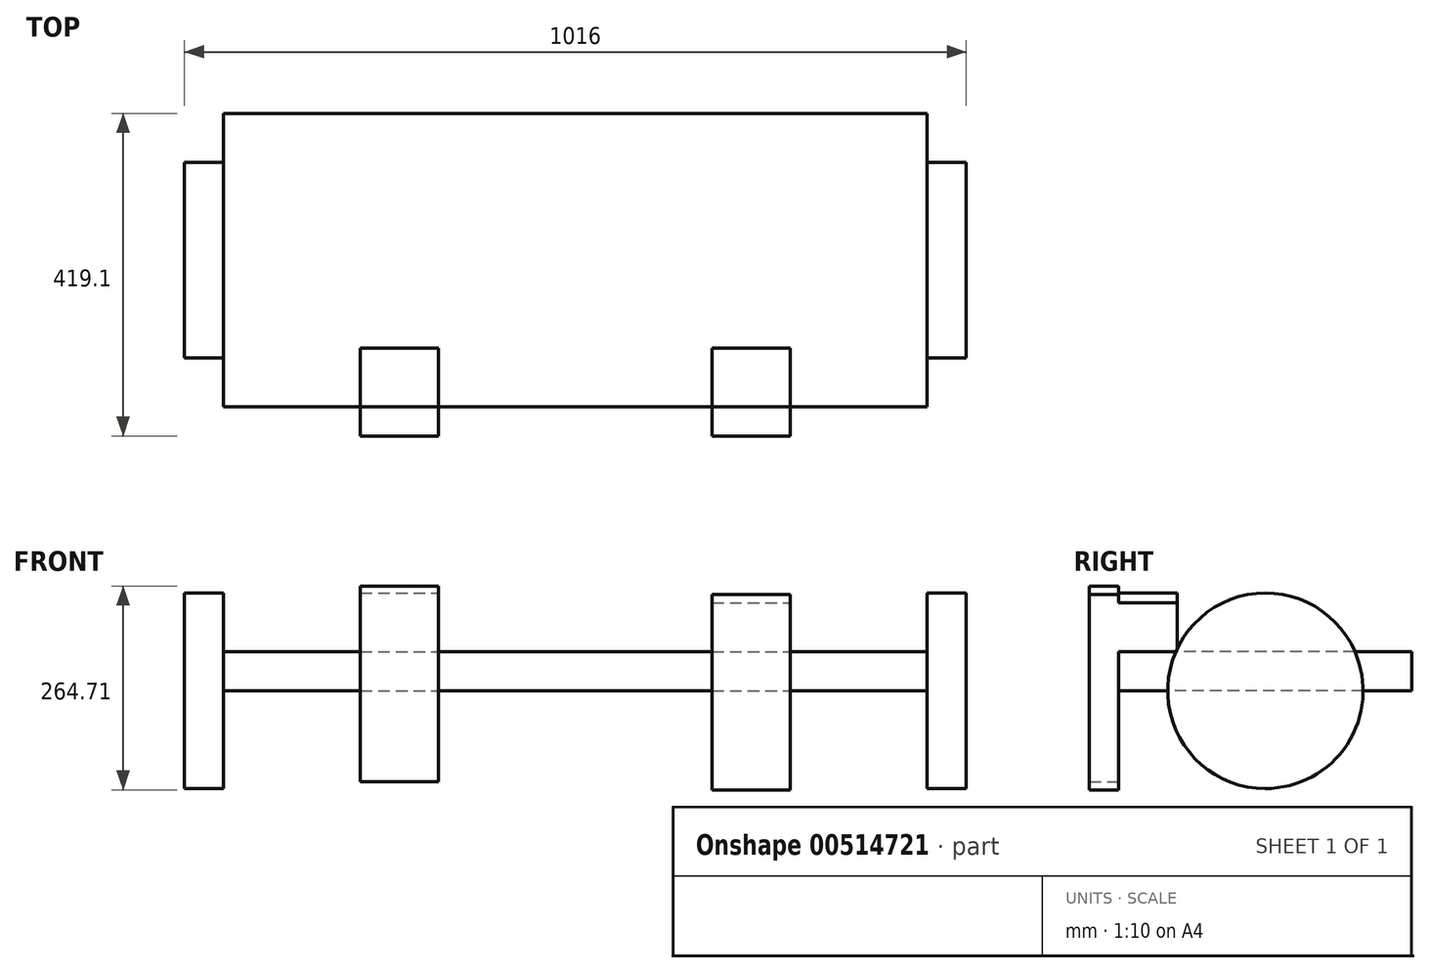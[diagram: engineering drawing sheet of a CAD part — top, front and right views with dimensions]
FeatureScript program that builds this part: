
annotation { "Feature Type Name" : "Feature", "Feature Type Description" : "" }
export const myFeature = defineFeature(function(context is Context, id is Id, definition is map)
    precondition{}
    {
        {
            var Q0;
            Q0=qCreatedBy(makeId("Top.planeOp"),FACE);
            var sketch = newSketch(context, id + "F0", { "sketchPlane" : qUnion([Q0])});
            skLineSegment(sketch, "E0.bottom", {"start": v(-455.9, 96.8) * mm, "end": v(458.5, 96.8) * mm});
            skLineSegment(sketch, "E0.top", {"start": v(-455.9, -284.2) * mm, "end": v(458.5, -284.2) * mm});
            skLineSegment(sketch, "E0.left", {"start": v(-455.9, 96.8) * mm, "end": v(-455.9, -284.2) * mm});
            skLineSegment(sketch, "E0.right", {"start": v(458.5, 96.8) * mm, "end": v(458.5, -284.2) * mm});
            skSolve(sketch);
        }
        {
            var Q0;
            Q0 = qSketchRegion(id + "F0", true);
            extrude(context, id + "F1", {"entities" : qUnion([Q0]), "depth" : 50.8 * mm, "offsetDistance" : 25.4 * mm});
        }
        {
            var Q0;
            Q0=makeQuery(id+"F1.opExtrude","SWEPT_FACE",FACE,{"disambiguationData":[OSD([sQuery(id+"F0.wireOp",EDGE,"E0.right")])]});
            var sketch = newSketch(context, id + "F2", { "sketchPlane" : qUnion([Q0])});
            skCircle(sketch, "E1", {"center": v(-93.7, 0) * mm, "radius": 127 * mm});
            skSolve(sketch);
        }
        {
            var Q0;
            Q0 = qSketchRegion(id + "F2", true);
            extrude(context, id + "F3", {"entities" : qUnion([Q0]), "operationType" : NewBodyOperationType.ADD, "depth" : 50.8 * mm, "offsetDistance" : 25.4 * mm});
        }
        {
            var Q0;
            Q0=makeQuery(id+"F1.opExtrude","SWEPT_FACE",FACE,{"disambiguationData":[OSD([sQuery(id+"F0.wireOp",EDGE,"E0.left")])]});
            var sketch = newSketch(context, id + "F4", { "sketchPlane" : qUnion([Q0])});
            skCircle(sketch, "E2", {"center": v(93.7, 0) * mm, "radius": 127 * mm});
            skSolve(sketch);
        }
        {
            var Q0;
            Q0 = qSketchRegion(id + "F4", true);
            extrude(context, id + "F5", {"entities" : qUnion([Q0]), "operationType" : NewBodyOperationType.ADD, "depth" : 50.8 * mm, "offsetDistance" : 25.4 * mm});
        }
        {
            var Q0;
            Q0=makeQuery(id+"F1.opExtrude","SWEPT_FACE",FACE,{"disambiguationData":[OSD([sQuery(id+"F0.wireOp",EDGE,"E0.top")])]});
            var sketch = newSketch(context, id + "F6", { "sketchPlane" : qUnion([Q0])});
            skLineSegment(sketch, "E3.bottom", {"start": v(-278.1, 136.13) * mm, "end": v(-176.5, 136.13) * mm});
            skLineSegment(sketch, "E3.top", {"start": v(-278.1, -117.87) * mm, "end": v(-176.5, -117.87) * mm});
            skLineSegment(sketch, "E3.left", {"start": v(-278.1, 136.13) * mm, "end": v(-278.1, -117.87) * mm});
            skLineSegment(sketch, "E3.right", {"start": v(-176.5, 136.13) * mm, "end": v(-176.5, -117.87) * mm});
            skLineSegment(sketch, "E4.bottom", {"start": v(179.1, 125.42) * mm, "end": v(280.7, 125.42) * mm});
            skLineSegment(sketch, "E4.top", {"start": v(179.1, -128.58) * mm, "end": v(280.7, -128.58) * mm});
            skLineSegment(sketch, "E4.left", {"start": v(179.1, 125.42) * mm, "end": v(179.1, -128.58) * mm});
            skLineSegment(sketch, "E4.right", {"start": v(280.7, 125.42) * mm, "end": v(280.7, -128.58) * mm});
            skSolve(sketch);
        }
        {
            var Q0;
            Q0 = qSketchRegion(id + "F6", true);
            extrude(context, id + "F7", {"entities" : qUnion([Q0]), "operationType" : NewBodyOperationType.ADD, "depth" : 38.1 * mm, "offsetDistance" : 25.4 * mm});
        }
        {
            var Q0;
            Q0=makeQuery(id+"F1.opExtrude","CAP_FACE",FACE,{"disambiguationData":[OSD([sQuery(id+"F0.wireOp",EDGE,"E0.bottom"),sQuery(id+"F0.wireOp",EDGE,"E0.top"),sQuery(id+"F0.wireOp",EDGE,"E0.left"),sQuery(id+"F0.wireOp",EDGE,"E0.right")])],"isStart":false});
            var sketch = newSketch(context, id + "F8", { "sketchPlane" : qUnion([Q0])});
            skLineSegment(sketch, "E5.bottom", {"start": v(-278.1, -284.2) * mm, "end": v(-176.5, -284.2) * mm});
            skLineSegment(sketch, "E5.top", {"start": v(-278.1, -208) * mm, "end": v(-176.5, -208) * mm});
            skLineSegment(sketch, "E5.left", {"start": v(-278.1, -284.2) * mm, "end": v(-278.1, -208) * mm});
            skLineSegment(sketch, "E5.right", {"start": v(-176.5, -284.2) * mm, "end": v(-176.5, -208) * mm});
            skSolve(sketch);
        }
        {
            var Q0;
            Q0 = qSketchRegion(id + "F8", true);
            extrude(context, id + "F9", {"entities" : qUnion([Q0]), "operationType" : NewBodyOperationType.ADD, "depth" : 76.2 * mm, "offsetDistance" : 25.4 * mm});
        }
        {
            var Q0;
            Q0=makeQuery(id+"F1.opExtrude","CAP_FACE",FACE,{"disambiguationData":[OSD([sQuery(id+"F0.wireOp",EDGE,"E0.bottom"),sQuery(id+"F0.wireOp",EDGE,"E0.top"),sQuery(id+"F0.wireOp",EDGE,"E0.left"),sQuery(id+"F0.wireOp",EDGE,"E0.right")])],"isStart":false});
            var sketch = newSketch(context, id + "F10", { "sketchPlane" : qUnion([Q0])});
            skLineSegment(sketch, "E6.bottom", {"start": v(179.1, -284.2) * mm, "end": v(280.7, -284.2) * mm});
            skLineSegment(sketch, "E6.top", {"start": v(179.1, -208) * mm, "end": v(280.7, -208) * mm});
            skLineSegment(sketch, "E6.left", {"start": v(179.1, -284.2) * mm, "end": v(179.1, -208) * mm});
            skLineSegment(sketch, "E6.right", {"start": v(280.7, -284.2) * mm, "end": v(280.7, -208) * mm});
            skSolve(sketch);
        }
        {
            var Q0;
            Q0 = qSketchRegion(id + "F10", true);
            extrude(context, id + "F11", {"entities" : qUnion([Q0]), "operationType" : NewBodyOperationType.ADD, "depth" : 63.5 * mm, "offsetDistance" : 25.4 * mm});
        }
    });
